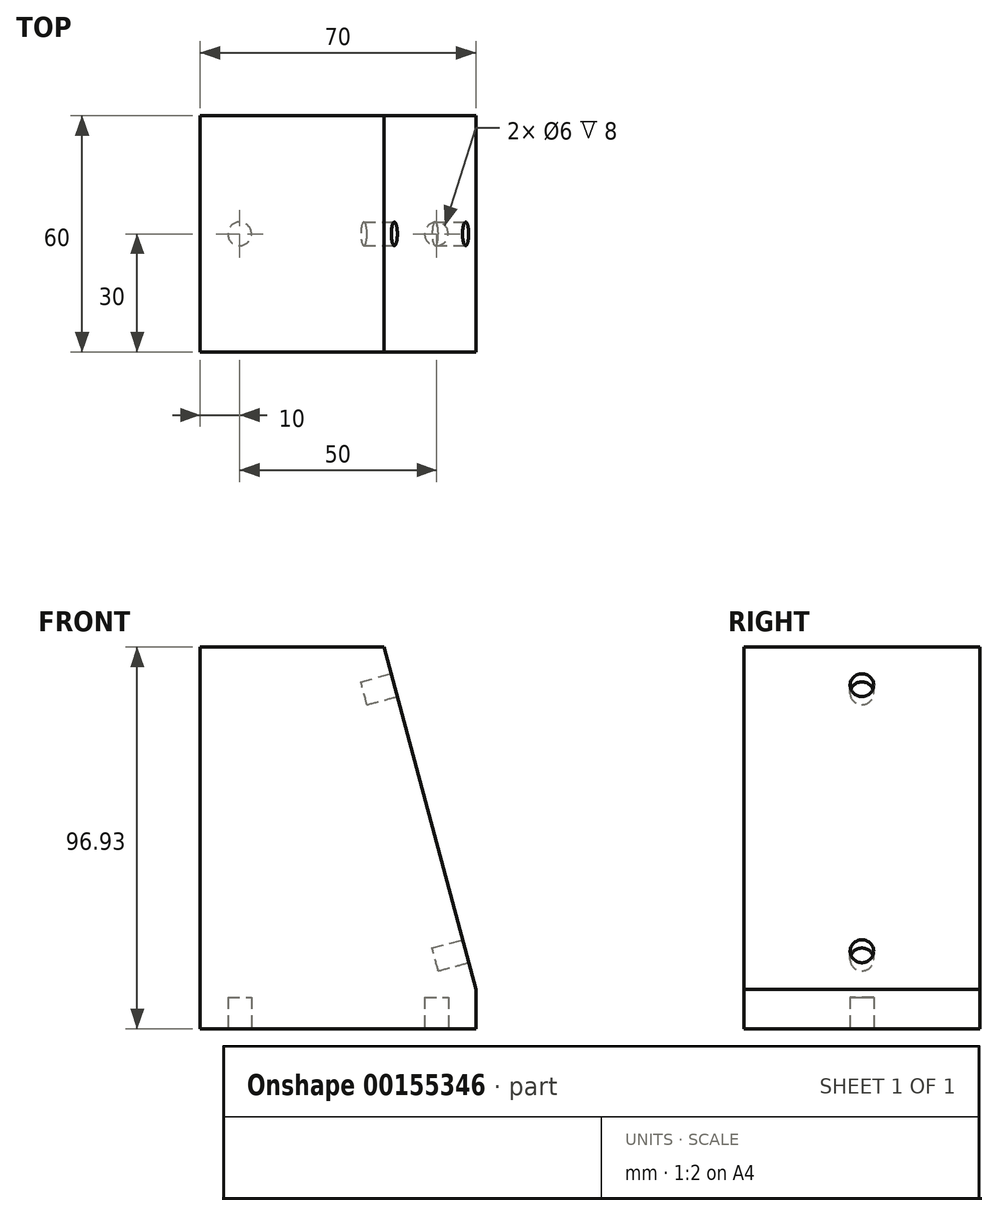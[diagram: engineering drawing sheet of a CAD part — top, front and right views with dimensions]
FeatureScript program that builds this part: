
annotation { "Feature Type Name" : "Feature", "Feature Type Description" : "" }
export const myFeature = defineFeature(function(context is Context, id is Id, definition is map)
    precondition{}
    {
        {
            var Q0;
            Q0=qCreatedBy(makeId("Front.planeOp"),FACE);
            var sketch = newSketch(context, id + "F0", { "sketchPlane" : qUnion([Q0])});
            skLineSegment(sketch, "E0", {"start": v(6.2, 86.93) * mm, "end": v(29.5, 0) * mm});
            skLineSegment(sketch, "E1.0", {"start": v(-40.5, -10) * mm, "end": v(29.5, -10) * mm});
            skLineSegment(sketch, "E2", {"start": v(29.5, -10) * mm, "end": v(29.5, 0) * mm});
            skLineSegment(sketch, "E3", {"start": v(0, 0) * mm, "end": v(59.5, 0) * mm, "construction": true});
            skLineSegment(sketch, "E4", {"start": v(6.2, 86.93) * mm, "end": v(-40.5, 86.93) * mm});
            skLineSegment(sketch, "E5", {"start": v(-40.5, -10) * mm, "end": v(-40.5, 86.93) * mm});
            skSolve(sketch);
        }
        {
            var Q0;
            Q0=makeQuery(id+"F0.imprint","IMPRINT",FACE,{"disambiguationData":[TD([[makeQuery(id+"F0.imprint","IMPRINT",EDGE,{"derivedFrom":sQuery(id+"F0.wireOp",EDGE,"9UmFtTPp-Rfgm-WyM1-NILj-WxgolYEMkt9n")}),-1.0]])]});
            var Q1;
            Q1=makeQuery(id+"F0.imprint","IMPRINT",FACE,{"disambiguationData":[TD([[makeQuery(id+"F0.imprint","IMPRINT",EDGE,{"derivedFrom":sQuery(id+"F0.wireOp",EDGE,"E0")}),-1.0]])]});
            extrude(context, id + "F1", {"entities" : qUnion([Q0, Q1]), "depth" : 60 * mm});
        }
        {
            var Q0;
            Q0=makeQuery(id+"F1.opExtrude","SWEPT_FACE",FACE,{"disambiguationData":[OSD([sQuery(id+"F0.wireOp",EDGE,"E1.0")])]});
            var sketch = newSketch(context, id + "F2", { "sketchPlane" : qUnion([Q0])});
            skLineSegment(sketch, "E6", {"start": v(-40.5, 30) * mm, "end": v(65.18, 30) * mm, "construction": true});
            skCircle(sketch, "E7", {"center": v(-30.5, 30) * mm, "radius": 3 * mm});
            skCircle(sketch, "E8", {"center": v(19.5, 30) * mm, "radius": 3 * mm});
            skSolve(sketch);
        }
        {
            var Q0;
            Q0 = qSketchRegion(id + "F2", true);
            extrude(context, id + "F3", {"entities" : qUnion([Q0]), "operationType" : NewBodyOperationType.REMOVE, "oppositeDirection" : true, "depth" : 8 * mm});
        }
        {
            var Q0;
            Q0=makeQuery(id+"F1.opExtrude","SWEPT_FACE",FACE,{"disambiguationData":[OSD([sQuery(id+"F0.wireOp",EDGE,"E0")])]});
            var sketch = newSketch(context, id + "F4", { "sketchPlane" : qUnion([Q0])});
            skLineSegment(sketch, "E9", {"start": v(-30, 82.36) * mm, "end": v(-30, -51.17) * mm, "construction": true});
            skCircle(sketch, "E10", {"center": v(-30, 72.36) * mm, "radius": 3 * mm});
            skCircle(sketch, "E11", {"center": v(-30, 2.36) * mm, "radius": 3 * mm});
            skSolve(sketch);
        }
        {
            var Q0;
            Q0 = qSketchRegion(id + "F4", true);
            extrude(context, id + "F5", {"entities" : qUnion([Q0]), "operationType" : NewBodyOperationType.REMOVE, "oppositeDirection" : true, "depth" : 8 * mm});
        }
    });
